# Revit family: Domotics-DomesticRanges-GEWISS-CHORUS_COMMAND-TWO-WAY_SWITCH_2M
name_source: partatom
category: Apparecchi elettrici
revit_build: Autodesk Revit 2016 (Build: 20161004_0715(x64)
units: mm (PartAtom-declared; Revit-internal decimal feet)

## family parameters
Condiviso = Sì
Host = Superficie
Mantenere orientamento annotazione = Sì
Numero OmniClass = 23.80.50.11.14
Punto di calcolo locali = Sì
Quota connettore circolare = Usa diametro
Taglio con vuoti quando caricato = No
Tipo di parte = Normale
Titolo OmniClass = Switches

## types (9) — shared parameters
Bidimensionale = bidimensionale deviatori 2m : GW12073
Breaking capacity: = 1.25 In (200 position changes)
Carico apparente = 0 VA
Catalogue = DOMOTICS
Catalogue Range = CHORUS - DOMESTIC RANGE
Category = Two-way switch
Electrocod = 0130
Glow Wire Test = 850°C
IDF = 1830170a-a286-4216-acdb-fdf4c4ea11f9
IDT = cf639209-7c62-4d14-8d44-b8a0a132f670
Immagine tipo = <Nessuno>
Insulation resistance = > 5 MOhm
Larghezza pulsante = 46 mm  [stored 0.150919 ft]
N poli = 1
No. Chorus modules = 2
Number of poles = 1P
Produttore = GEWISS S.p.A.
Prolonged operation (no.of position changes) = 40.000 at In 250 V ac cosÃ˜=0,6
Prospetto di default = 1219 mm
Resistance at test voltage = 2000 V at 50 Hz for 1 minute
SEO = 2 way switch
Simbolo = SIMBOLO DEVIATORI : DEV1PLUM
Standard; = EN 60669-1
Technical sheet = https://www.gewiss.com
Terminal grip on cable traction = > 50 N
Terminal tightening capacity flexible cables (mm2) = min. 0,75 - max. 2x4
Terminal tightening capacity rigid cables (mm2) = min. 0,5 - max. 2x2,5
Thermo-pressure with ball = 125
Tipo_ = CHORUS DEVIATORI 2M_BASE : GW14073 - Titanio - Illuminabile segnalazione
URL = https://www.gewiss.com
Version file RFA = 19.0
Volt = 230 V
Voltage = 250 V ac
Voltage: = 250 V ac
Wiring terminals = With screw

## per-type parameters (varying)
| type | Button key | Colour | Description: | Descrizione | EAN code | Modello | Type |
| GW14073 - Titanium - Illuminable | With replaceable neutral lens | Titanium | 1P - 16AX illuminable | 2-WAY SWITCH 2M 1P 16AX ILL SIG TITANIUM | 8011564265639 | GW14073 | Indicator |
| GW10072 - White - Illuminable | With diffuser | White | 1P - 16AX illuminable | 2-WAY SWITCH, 2M 1P 16AX ILL LOC WHITE | 8011564257382 | GW10072 | Backlit |
| GW12073 - Black - Illuminable | With replaceable neutral lens | Black | 1P - 16AX illuminable | 2-WAY SWITCH, 2M 1P 16AX ILL SIG BLACK | 8011564269378 | GW12073 | Indicator |
| GW12072 - Black - Illuminable | With diffuser | Black | 1P - 16AX illuminable | 2-WAY SWITCH, 2M 1P 16AX ILL LOC BLACK | 8011564269361 | GW12072 | Backlit |
| GW10073 - White - Illuminable | With replaceable neutral lens | White | 1P - 16AX illuminable | 2-WAY SWITCH, 2M 1P 16AX ILL SIG WHITE | 8011564257405 | GW10073 | Indicator |
| GW14071 - Titanium | Neutral | Titanium | 1P - 16AX | 2-WAY SWITCH, 2M 1P 16AX TITANIUM | 8011564265592 | GW14071 | General |
| GW12071 - Black | Neutral | Black | 1P - 16AX | 2-WAY SWITCH, 2M 1P 16AX BLACK | 8011564269354 | GW12071 | General |
| GW10071 - White | Neutral | White | 1P - 16AX | 2-WAY SWITCH, 2M 1P 16AX WHITE | 8011564257368 | GW10071 | General |
| GW14072 - Titanium - Illuminable | With diffuser | Titanium | 1P - 16AX illuminable | 2-WAY SWITCH 2M 1P 16AX ILL LOC TITANIUM | 8011564265615 | GW14072 | Backlit |

note: source unit labels omitted for Thermo-pressure with ball — the stored unit's dimension contradicts the parameter name (converter mislabeling)

note: [stored X ft] marks values corroborated as IEEE doubles in the binary element streams (Revit-internal decimal feet)

## geometry (parser evidence)
native form markers: Sweep x1
no freeform markers — native parametric forms only
